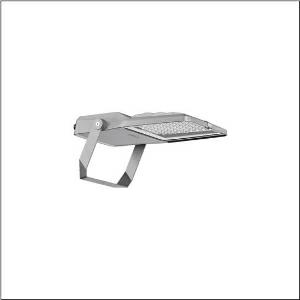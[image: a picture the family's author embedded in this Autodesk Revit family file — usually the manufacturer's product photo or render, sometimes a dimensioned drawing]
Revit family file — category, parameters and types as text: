
# Revit family: floodlight_fl_21_iq_mini___rs12_5xa7772d5b1a_d30b
name_source: partatom
category: Lighting Fixtures
units: mm (PartAtom-declared; Revit-internal decimal feet)

## family parameters
Cut with Voids When Loaded = No
Host = Face
Light Source = No
Part Type = Normal
Room Calculation Point = No
Round Connector Dimension = Use Diameter
Shared = No

## types (1)
- --- (1 x LED, 16820 lm, 143 W, 4000K)
    Apparent Load = 143 VA
    CIE Flux Codes = 79 92 99 100 100
    Color Rendering = 80
    Color Temperature = 4000K
    Default Elevation = 1800 mm
    Description = Floodlight FL 21 iQ mini, floodlight, primary light control with lens, of PMMA, primary optical cover: protective disc, of toughened safety glass, transparent, light distribution: RS12, light emission: direct distribution, installation type: surface-mounted, LED, High Power LED, rated luminous flux: 16.820lm, luminous efficacy: 118lm/W, light colour: 840, colour temperature: 4000K, control gear: iQ Street-Remote/DALI, control: Street-Remote, Auto-Match, Temp-Guard, Night-Set, Smart-Wire, Desk-Remote (wireless, voltage-free reading and setting of iQ features in the workshop via application-optimized NFC function/RFID function), optimised constant luminous flux control (CLO 2.0), with terminal, 6-pole, mains connection: 220..240V, AC, 50/60Hz, start of lifetime: 143W, end of service life: 152W, reduction: 61W, luminaire housing, of diecast aluminium, powder-coated, Siteco® metallic grey (DB 702S), corrosivity category C5 mid according to DIN EN ISO 12944, suitable for swimming pools, chlorine-resistant, sealing non-destructively replaceable, mounting bracket, of steel, galvanised, powder-coated, Siteco® metallic grey (DB 702S), protection rating (complete): IP66, insulation class (complete): insulation class II (safety insulation), certification: CE, ENEC, VDE, protection symbol: D, impact resistance: IK08, permissible operating ambient temperature: -40..+40°C, permissible operating ambient temperature for outdoor applications: -40..+50°C, standard: DIN EN 12944, LABS conformity tested according to VDMA 24364:2018-05, packaging unit: 1 piece

Light Distribution: RS12
    Height = 70 mm
    Lamp = 1 x LED
    Lamp Light Flux = 16820 lm
    Lamp Power = 143 W
    Lamp count = 1
    Length = 485 mm
    Luminous efficacy = 118 lm/W
    Manufacturer = Siteco
    ModVariant = No
    Model = 5XA7772D5B1A
    Number of Poles = 1
    OnlyDefault = Yes
    Power Factor = 1
    Product Name = Floodlight FL 21 iQ mini | RS12
    Product group = floodlight | pylon annexe
    ProductGroupID = 6200
    Protection Class = Protection class II
    Protection Degree = IP 66
    RLX_Detail_Level = 1
    RLX_Emergency_Light_Flux = 0 lm
    RLX_Emergency_Type = 0
    RLX_Emergency_Type_DB = No
    RlxData = <blob elided: 91489 chars, md5=dfd35405>
    Socket = socket
    Standby Power = 0 W
    System Light Flux = 16820 lm
    System Power = 143 W
    Type Comments = factory setting: luminous flux: 100 % | dim-lin: 254 | 730 mA
    Type Image = l_1006845.jpg
    URL = http://relux.com
    VarID = @adj_167262
    Voltage = 0 V
    Weight = 0.00 kg
    Width = 337 mm

## geometry (parser evidence)
native form markers: Blend x4, Sweep x15
no freeform markers — native parametric forms only
